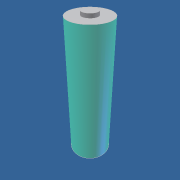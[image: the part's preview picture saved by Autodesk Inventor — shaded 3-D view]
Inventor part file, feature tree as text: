
AUTODESK INVENTOR PART (.ipt)
format: ipt  version: unknown  size: 177,152 bytes
history: native  units: mm
features: extrude x3, sketch x3
ambient origin geometry x8: Origin, YZ Plane, XZ Plane, XY Plane, X Axis, Y Axis, Z Axis, Center Point
bodies: Solid1 (feature_tree)
feature tree (6):
  extrude  "Extrusion1"  Depth=48.2mm TaperAngle=0.0deg
  extrude  "Extrusion2"  Depth=1.3mm TaperAngle=0.0deg
  extrude  "Extrusion3"  Depth=0.75mm TaperAngle=0.0deg
  sketch  "Sketch1"  dims[d0=14.0mm d1=48.2mm d2=0.0mm]
  sketch  "Sketch2"  dims[d3=5.2mm d4=1.3mm d5=0.0mm]
  sketch  "Sketch3"  dims[d6=8.53mm d7=0.75mm d8=0.0mm]
